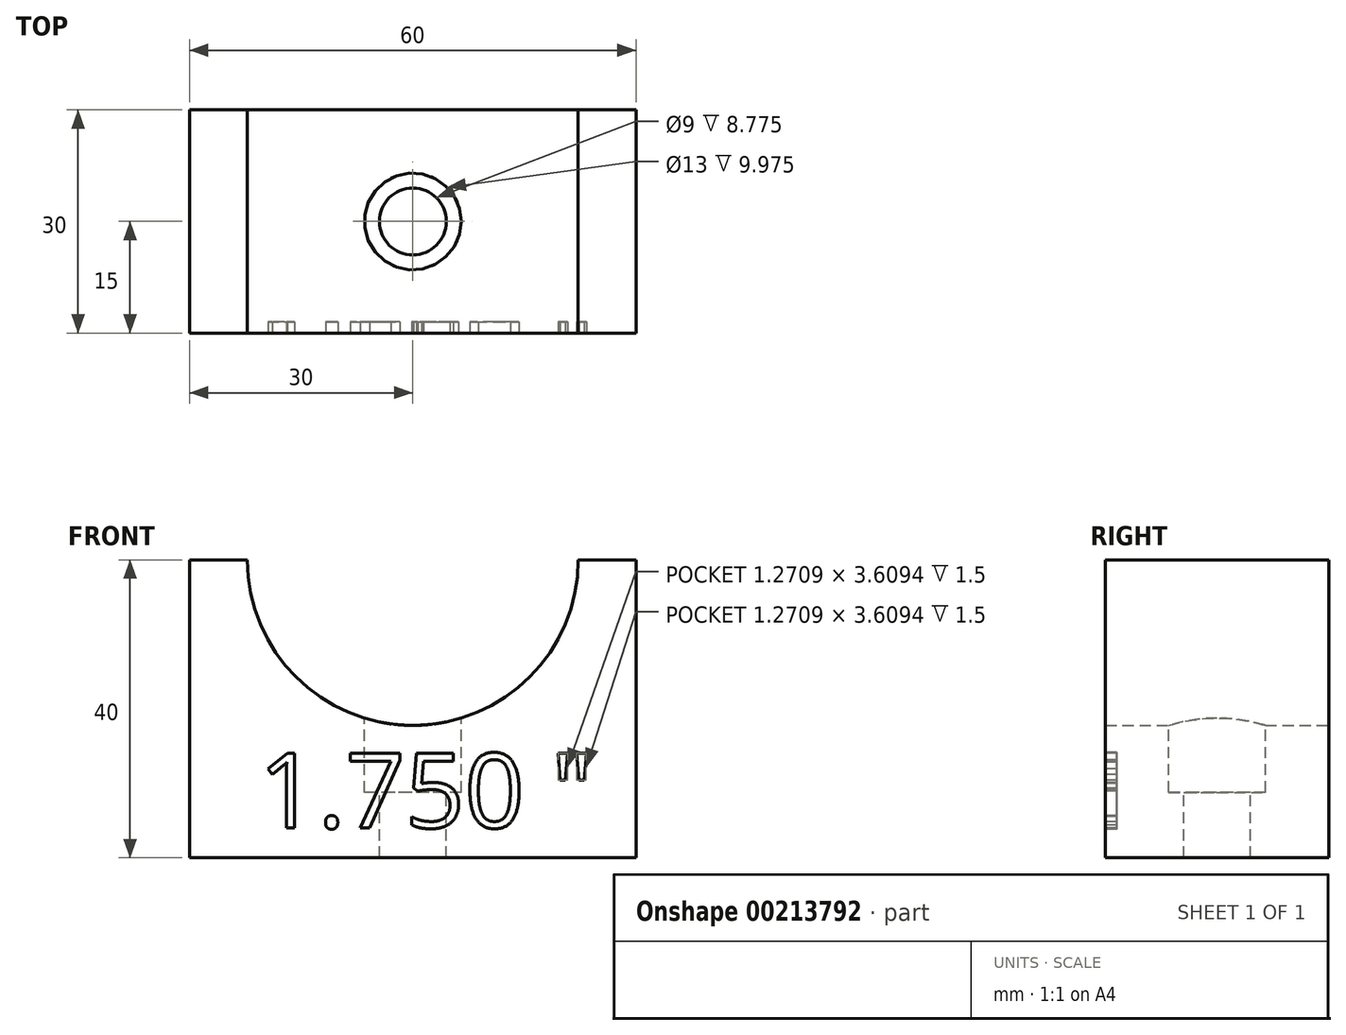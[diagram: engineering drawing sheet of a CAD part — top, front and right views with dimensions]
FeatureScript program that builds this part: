
annotation { "Feature Type Name" : "Feature", "Feature Type Description" : "" }
export const myFeature = defineFeature(function(context is Context, id is Id, definition is map)
    precondition{}
    {
        {
            var Q0;
            Q0=qCreatedBy(makeId("Front.planeOp"),FACE);
            var sketch = newSketch(context, id + "F0", { "sketchPlane" : qUnion([Q0])});
            skLineSegment(sketch, "E0.bottom", {"start": v(30, -20) * mm, "end": v(-30, -20) * mm});
            skLineSegment(sketch, "E0.top", {"start": v(30, 20) * mm, "end": v(-30, 20) * mm});
            skLineSegment(sketch, "E0.left", {"start": v(30, -20) * mm, "end": v(30, 20) * mm});
            skLineSegment(sketch, "E0.right", {"start": v(-30, -20) * mm, "end": v(-30, 20) * mm});
            skPoint(sketch, "E0.middle", {"position": v(0, 0) * mm});
            skLineSegment(sketch, "E1", {"start": v(0, 0) * mm, "end": v(0, 20) * mm});
            skPoint(sketch, "E2", {"position": v(0, 20) * mm});
            skCircle(sketch, "E3", {"center": v(0, 20) * mm, "radius": 22.23 * mm});
            skSolve(sketch);
        }
        {
            var Q0;
            Q0=makeQuery(id+"F0.imprint","IMPRINT",FACE,{"disambiguationData":[TD([[makeQuery(id+"F0.imprint","IMPRINT",EDGE,{"derivedFrom":sQuery(id+"F0.wireOp",EDGE,"E0.bottom")}),-1.0]])]});
            extrude(context, id + "F1", {"entities" : qUnion([Q0]), "depth" : 30 * mm});
        }
        {
            var Q0;
            Q0=qCreatedBy(makeId("Top.planeOp"),FACE);
            var sketch = newSketch(context, id + "F2", { "sketchPlane" : qUnion([Q0])});
            skLineSegment(sketch, "E4", {"start": v(0, 0) * mm, "end": v(0, -30) * mm});
            skPoint(sketch, "E5", {"position": v(0, -15) * mm});
            skSolve(sketch);
        }
        {
            var Q0;
            Q0=sQuery(id+"F2.wireOp",VERTEX,"E5");
            var Q1;
            Q1=makeQuery(id+"F1.opExtrude","SWEPT_BODY",BODY,{"disambiguationData":[OSD([sQuery(id+"F0.wireOp",EDGE,"E0.bottom"),sQuery(id+"F0.wireOp",EDGE,"E0.top"),sQuery(id+"F0.wireOp",EDGE,"E0.left"),sQuery(id+"F0.wireOp",EDGE,"E0.right"),sQuery(id+"F0.wireOp",EDGE,"E3")])]});
            hole(context, id + "F3", {"style" : HoleStyle.C_BORE, "endStyle" : HoleEndStyle.THROUGH, "holeDiameter" : 9 * mm, "cBoreDiameter" : 13 * mm, "cBoreDepth" : 9 * mm, "locations" : qUnion([Q0]), "scope" : qUnion([Q1]), "isTappedThrough" : true});
        }
        {
            var Q0;
            Q0=makeQuery(id+"F1.opExtrude","CAP_FACE",FACE,{"disambiguationData":[OSD([sQuery(id+"F0.wireOp",EDGE,"E0.bottom"),sQuery(id+"F0.wireOp",EDGE,"E0.top"),sQuery(id+"F0.wireOp",EDGE,"E0.left"),sQuery(id+"F0.wireOp",EDGE,"E0.right"),sQuery(id+"F0.wireOp",EDGE,"E3")])],"isStart":false});
            var sketch = newSketch(context, id + "F4", { "sketchPlane" : qUnion([Q0])});
            skText(sketch, "E6", { "text": "1.750 \"", "fontName": "OpenSans-Regular.ttf"});
            const initialGuessF4  = {"E6": [-0.02077, -0.016, 1, 0, 0.01008]};
            skSetInitialGuess(sketch, initialGuessF4);
            skSolve(sketch);
        }
        {
            var Q0;
            Q0 = qSketchRegion(id + "F4", true);
            extrude(context, id + "F5", {"entities" : qUnion([Q0]), "operationType" : NewBodyOperationType.REMOVE, "oppositeDirection" : true, "depth" : 1.5 * mm});
        }
    });
